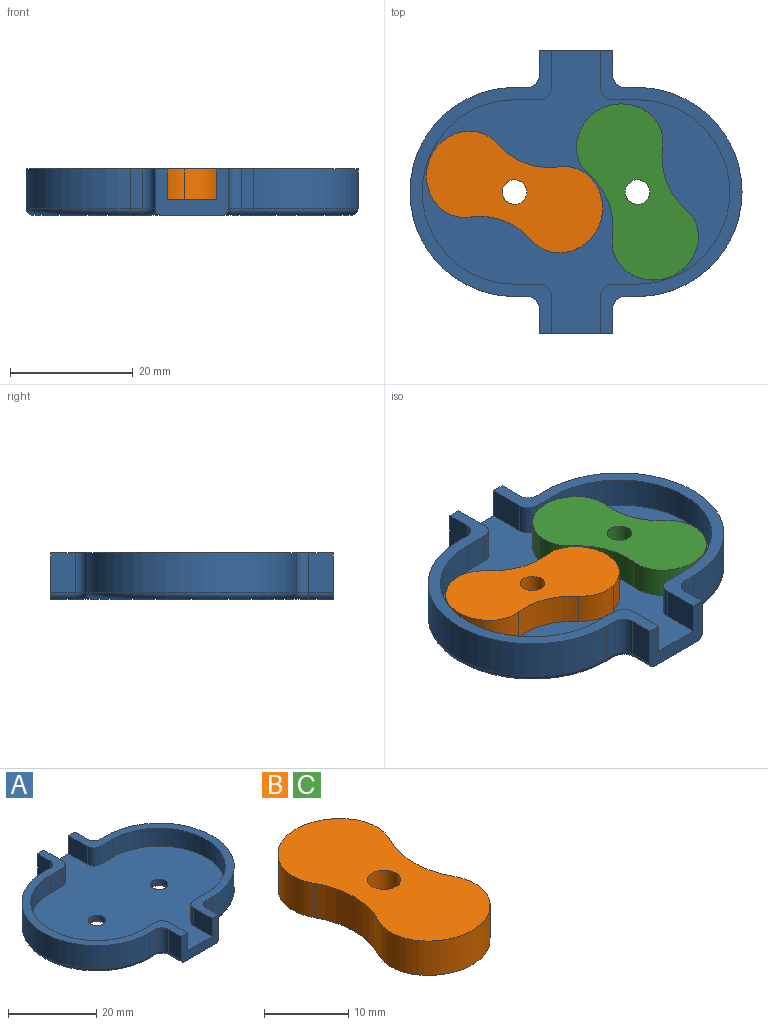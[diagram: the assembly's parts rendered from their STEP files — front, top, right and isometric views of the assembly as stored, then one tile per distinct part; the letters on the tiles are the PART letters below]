
ASSEMBLY  parts=3 mates=2
PART A: 56 faces, bbox 56.8x46x7.5 mm
  f0: plane 50x46mm, normal (0,0,1), area 1413.2mm2, adj f1,f7,f12,f14,f16,f17,f18,f19
  f1: plane 12x7.5mm, normal (0,-1,0), area 49.6mm2, adj f0,f2,f13,f15,f16,f21,f26,f27
  f2: plane 6.5x4mm, normal (1,0,0), area 26mm2, adj f1,f27,f34,f42
  f3: plane 6.5x2mm, normal (0,-1,0), area 13mm2, adj f4,f27,f34,f40
  f4: cylinder r=17mm len=34mm, axis (0,0,1), area 347.1mm2, adj f3,f5,f27,f39
  f5: plane 6.5x2mm, normal (0,1,0), area 13mm2, adj f4,f27,f35,f38
  f6: plane 6.5x4mm, normal (1,0,0), area 26mm2, adj f7,f27,f35,f36
  f7: plane 12x7.5mm, normal (0,1,0), area 49.6mm2, adj f0,f6,f8,f15,f20,f21,f22,f27
  f8: plane 6.5x4mm, normal (-1,0,0), area 26mm2, adj f7,f21,f32,f49
  f9: plane 6.5x2mm, normal (0,1,0), area 13mm2, adj f10,f21,f32,f47
  f10: cylinder r=17mm len=34mm, axis (0,0,1), area 347.1mm2, adj f9,f11,f21,f46
  f11: plane 6.5x2mm, normal (0,-1,0), area 13mm2, adj f10,f21,f33,f45
  f12: cylinder r=2mm len=4mm, axis (0,0,1), area 17.5mm2, adj f0,f53
  f13: plane 6.5x4mm, normal (-1,0,0), area 26mm2, adj f1,f21,f33,f43
  f14: cylinder r=2mm len=4mm, axis (0,0,1), area 17.5mm2, adj f0,f52
  f15: plane 52x46mm, normal (0,0,-1), area 1531.5mm2, adj f1,f7,f36,f37,f38,f39,f40,f41
  f16: plane 6x5mm, normal (1,0,0), area 30mm2, adj f0,f1,f21,f31
  f17: plane 5x4mm, normal (0,1,0), area 20mm2, adj f0,f18,f21,f31
  f18: cylinder r=15mm len=30mm, axis (0,0,-1), area 235.6mm2, adj f0,f17,f19,f21
  f19: plane 5x4mm, normal (0,-1,0), area 20mm2, adj f0,f18,f21,f30
  f20: plane 6x5mm, normal (1,0,0), area 30mm2, adj f0,f7,f21,f30
  f21: plane 46x23mm, normal (0,0,1), area 148.5mm2, adj f1,f7,f8,f9,f10,f11,f13,f16
  f22: plane 6x5mm, normal (-1,0,0), area 30mm2, adj f0,f7,f27,f28
  f23: plane 5x4mm, normal (0,-1,0), area 20mm2, adj f0,f24,f27,f28
  f24: cylinder r=15mm len=30mm, axis (0,0,-1), area 235.6mm2, adj f0,f23,f25,f27
  f25: plane 5x4mm, normal (0,1,0), area 20mm2, adj f0,f24,f27,f29
  f26: plane 6x5mm, normal (-1,0,0), area 30mm2, adj f0,f1,f27,f29
  f27: plane 46x23mm, normal (0,0,1), area 148.5mm2, adj f1,f2,f3,f4,f5,f6,f7,f22
  f28: cylinder r=2mm len=5mm, axis (0,0,-1), area 15.7mm2, adj f0,f22,f23,f27
  f29: cylinder r=2mm len=5mm, axis (0,0,1), area 15.7mm2, adj f0,f25,f26,f27
  f30: cylinder r=2mm len=5mm, axis (0,0,1), area 15.7mm2, adj f0,f19,f20,f21
  f31: cylinder r=2mm len=5mm, axis (0,0,-1), area 15.7mm2, adj f0,f16,f17,f21
  f32: cylinder r=2mm len=6.5mm, axis (0,0,-1), area 20.4mm2, adj f8,f9,f21,f48
  f33: cylinder r=2mm len=6.5mm, axis (0,0,-1), area 20.4mm2, adj f11,f13,f21,f44
  f34: cylinder r=2mm len=6.5mm, axis (0,0,-1), area 20.4mm2, adj f2,f3,f27,f41
  f35: cylinder r=2mm len=6.5mm, axis (0,0,-1), area 20.4mm2, adj f5,f6,f27,f37
  f36: cylinder r=1mm len=4mm, axis (0,-1,0), area 6.3mm2, adj f6,f7,f15,f37
  f37: torus R=3mm, axis (0,0,1), area 5.8mm2, adj f15,f35,f36,f38
  f38: cylinder r=1mm len=2mm, axis (1,0,0), area 3.1mm2, adj f5,f15,f37,f39
  f39: torus R=16mm, axis (0,0,1), area 82.1mm2, adj f4,f15,f38,f40
  f40: cylinder r=1mm len=2mm, axis (-1,0,0), area 3.1mm2, adj f3,f15,f39,f41
  f41: torus R=3mm, axis (0,0,1), area 5.8mm2, adj f15,f34,f40,f42
  f42: cylinder r=1mm len=4mm, axis (0,-1,0), area 6.3mm2, adj f1,f2,f15,f41
  f43: cylinder r=1mm len=4mm, axis (0,1,0), area 6.3mm2, adj f1,f13,f15,f44
  f44: torus R=3mm, axis (0,0,1), area 5.8mm2, adj f15,f33,f43,f45
  f45: cylinder r=1mm len=2mm, axis (-1,0,0), area 3.1mm2, adj f11,f15,f44,f46
  f46: torus R=16mm, axis (0,0,1), area 82.1mm2, adj f10,f15,f45,f47
  f47: cylinder r=1mm len=2mm, axis (1,0,0), area 3.1mm2, adj f9,f15,f46,f48
  f48: torus R=3mm, axis (0,0,1), area 5.8mm2, adj f15,f32,f47,f49
  f49: cylinder r=1mm len=4mm, axis (0,1,0), area 6.3mm2, adj f7,f8,f15,f48
  f50: cone r=3mm half-angle=45deg, axis (0,0,-1), area 19mm2, adj f53,f54
  f51: cone r=2mm half-angle=45deg, axis (0,0,-1), area 19mm2, adj f52,f55
  f52: torus R=2.25mm, axis (0,0,1), area 2.5mm2, adj f14,f51
  f53: torus R=2.25mm, axis (0,0,1), area 2.5mm2, adj f12,f50
  f54: torus R=3.1mm, axis (0,0,1), area 3.7mm2, adj f15,f50
  f55: torus R=3.1mm, axis (0,0,1), area 3.7mm2, adj f15,f51
PART B: 11 faces, bbox 14.2x29.6x5 mm
  f0: cylinder r=11.21mm len=10.72mm, axis (0,0,-1), area 55.9mm2, adj f5,f6,f7,f9
  f1: cylinder r=7.34mm len=12mm, axis (0,0,-1), area 70.2mm2, adj f5,f6,f7,f8
  f2: cylinder r=11.21mm len=10.72mm, axis (0,0,-1), area 55.9mm2, adj f5,f6,f8,f10
  f3: cylinder r=7.34mm len=12mm, axis (0,0,-1), area 70.2mm2, adj f5,f6,f9,f10
  f4: cylinder r=2mm len=5mm, axis (0,0,-1), area 62.8mm2, adj f5,f6
  f5: plane 29.6x14.19mm, normal (0,0,1), area 328.6mm2, adj f0,f1,f2,f3,f4,f7,f8,f9
  f6: plane 29.6x14.19mm, normal (0,0,-1), area 328.6mm2, adj f0,f1,f2,f3,f4,f7,f8,f9
  f7: cylinder r=6mm len=6.33mm, axis (0,0,1), area 33.4mm2, adj f0,f1,f5,f6
  f8: cylinder r=6mm len=6.33mm, axis (0,0,1), area 33.4mm2, adj f1,f2,f5,f6
  f9: cylinder r=6mm len=6.33mm, axis (0,0,1), area 33.4mm2, adj f0,f3,f5,f6
  f10: cylinder r=6mm len=6.33mm, axis (0,0,1), area 33.4mm2, adj f2,f3,f5,f6
PART C: same geometry as B
PLACE A at identity fixed
PLACE B rot(axis=(0,0,1),69.5deg) t=(-31.01,-56.2,0)mm
PLACE C rot(axis=(0,0,1),20.5deg) t=(-46.2,-21.01,0)mm
MATE revolute B.f4 <-> A.f14  axis (0,0,-1) through (-10,0,0)mm
MATE revolute A.f12 <-> C.f4  axis (0,0,1) through (10,0,0)mm
